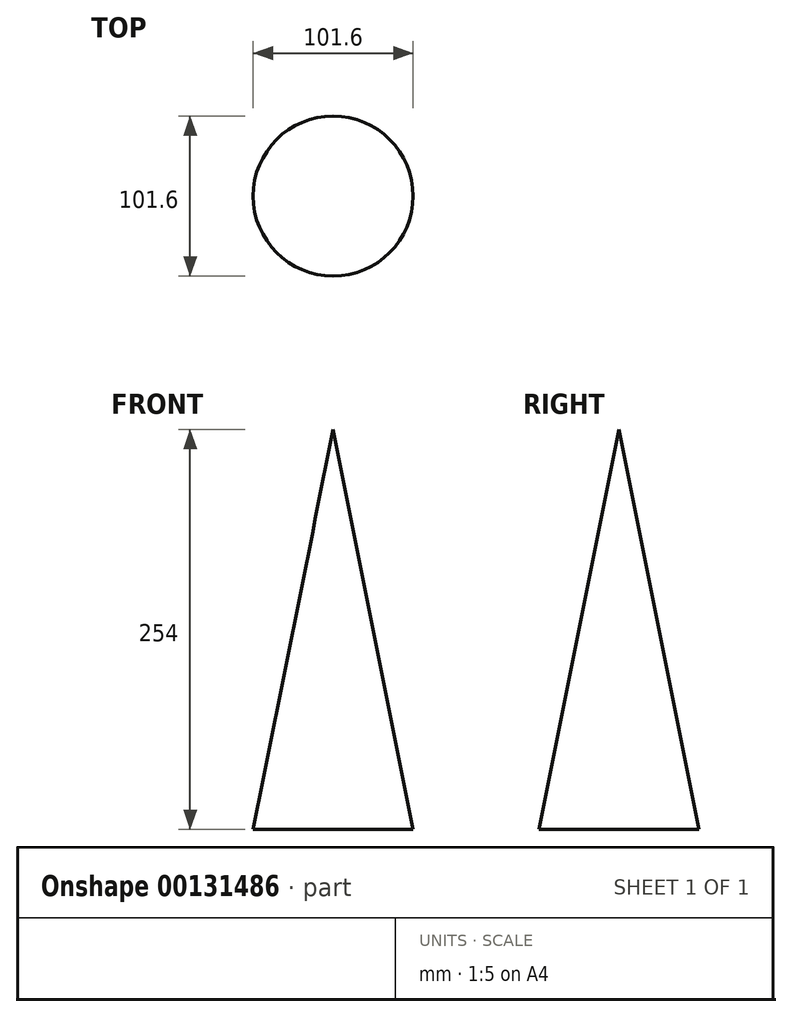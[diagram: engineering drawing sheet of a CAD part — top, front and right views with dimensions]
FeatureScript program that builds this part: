
annotation { "Feature Type Name" : "Feature", "Feature Type Description" : "" }
export const myFeature = defineFeature(function(context is Context, id is Id, definition is map)
    precondition{}
    {
        {
            var Q0;
            Q0=qCreatedBy(makeId("Front.planeOp"),FACE);
            var sketch = newSketch(context, id + "F0", { "sketchPlane" : qUnion([Q0])});
            skLineSegment(sketch, "E0", {"start": v(-50.8, 0) * mm, "end": v(0, 254) * mm});
            skLineSegment(sketch, "E1", {"start": v(-50.8, 0) * mm, "end": v(0, 0) * mm});
            skLineSegment(sketch, "E2", {"start": v(0, 0) * mm, "end": v(0, 254) * mm});
            skSolve(sketch);
        }
        {
            var Q0;
            Q0=makeQuery(id+"F0.imprint","IMPRINT",FACE,{"disambiguationData":[TD([[makeQuery(id+"F0.imprint","IMPRINT",EDGE,{"derivedFrom":sQuery(id+"F0.wireOp",EDGE,"E0")}),-1.0]])]});
            var Q1;
            Q1=sQuery(id+"F0.wireOp",EDGE,"E2");
            revolve(context, id + "F1", {"entities" : qUnion([Q0]), "axis" : qUnion([Q1]), "revolveType" : RevolveType.FULL});
        }
    });
